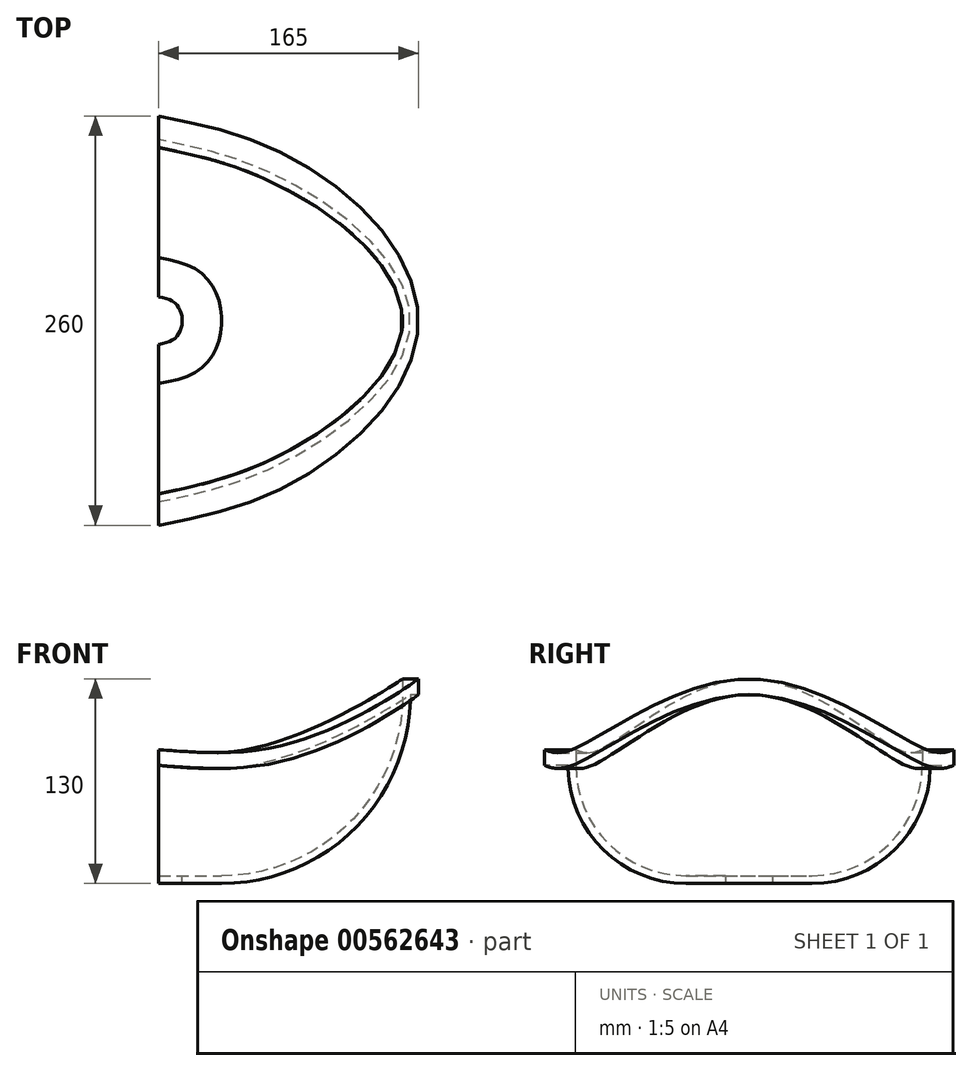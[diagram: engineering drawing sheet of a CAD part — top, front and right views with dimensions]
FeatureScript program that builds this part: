
annotation { "Feature Type Name" : "Feature", "Feature Type Description" : "" }
export const myFeature = defineFeature(function(context is Context, id is Id, definition is map)
    precondition{}
    {
        {
            var Q0;
            Q0=qCreatedBy(makeId("Front.planeOp"),FACE);
            var sketch = newSketch(context, id + "F0", { "sketchPlane" : qUnion([Q0])});
            skLineSegment(sketch, "E0.bottom", {"start": v(15, 5) * mm, "end": v(40, 5) * mm});
            skLineSegment(sketch, "E0.top", {"start": v(15, 0) * mm, "end": v(40, 0) * mm});
            skLineSegment(sketch, "E0.left", {"start": v(15, 5) * mm, "end": v(15, 0) * mm});
            skLineSegment(sketch, "E0.right", {"start": v(40, 5) * mm, "end": v(40, 0) * mm, "construction": true});
            skLineSegment(sketch, "E1.bottom", {"start": v(155, 130) * mm, "end": v(165, 130) * mm});
            skLineSegment(sketch, "E1.top", {"start": v(160, 120) * mm, "end": v(165, 120) * mm});
            skLineSegment(sketch, "E1.left", {"start": v(155, 130) * mm, "end": v(155, 120) * mm});
            skLineSegment(sketch, "E1.right", {"start": v(165, 130) * mm, "end": v(165, 120) * mm});
            skArc(sketch, "E2", {"start": v(40, 0) * mm, "mid": v(124.85, 35.15) * mm, "end": v(160, 120) * mm});
            skArc(sketch, "E3", {"start": v(40, 5) * mm, "mid": v(121.32, 38.68) * mm, "end": v(155, 120) * mm});
            skLineSegment(sketch, "E4", {"start": v(0, 0) * mm, "end": v(0, 50) * mm, "construction": true});
            skSolve(sketch);
        }
        {
            var Q0;
            Q0=sQuery(id+"F0.wireOp",EDGE,"E4");
            cPlane(context, id + "F1", {"entities" : qUnion([Q0]), "cplaneType" : CPlaneType.LINE_ANGLE, "offset" : 25 * mm, "angle" : 30 * degree, "oppositeDirection" : true, "width" : 150 * mm, "height" : 150 * mm});
        }
        {
            var Q0;
            Q0=qCreatedBy(id+"F1.planeOp",FACE);
            var sketch = newSketch(context, id + "F2", { "sketchPlane" : qUnion([Q0])});
            skLineSegment(sketch, "E5.bottom", {"start": v(15, 5) * mm, "end": v(40, 5) * mm});
            skLineSegment(sketch, "E5.top", {"start": v(15, 0) * mm, "end": v(40, 0) * mm});
            skLineSegment(sketch, "E5.left", {"start": v(15, 5) * mm, "end": v(15, 0) * mm});
            skLineSegment(sketch, "E5.right", {"start": v(40, 5) * mm, "end": v(40, 0) * mm, "construction": true});
            skLineSegment(sketch, "E6.bottom", {"start": v(110, 85) * mm, "end": v(130, 85) * mm});
            skLineSegment(sketch, "E6.top", {"start": v(115, 75) * mm, "end": v(130, 75) * mm});
            skLineSegment(sketch, "E6.left", {"start": v(110, 85) * mm, "end": v(110, 75) * mm});
            skLineSegment(sketch, "E6.right", {"start": v(130, 85) * mm, "end": v(130, 75) * mm});
            skArc(sketch, "E7", {"start": v(40, 0) * mm, "mid": v(93.03, 21.97) * mm, "end": v(115, 75) * mm});
            skArc(sketch, "E8", {"start": v(40, 5) * mm, "mid": v(89.5, 25.5) * mm, "end": v(110, 75) * mm});
            skLineSegment(sketch, "E9", {"start": v(0, 0) * mm, "end": v(0, 50) * mm, "construction": true});
            skSolve(sketch);
        }
        {
            var Q0;
            Q0=sQuery(id+"F2.wireOp",EDGE,"E9");
            cPlane(context, id + "F3", {"entities" : qUnion([Q0]), "cplaneType" : CPlaneType.LINE_ANGLE, "offset" : 25 * mm, "angle" : 150 * degree, "oppositeDirection" : true, "width" : 150 * mm, "height" : 150 * mm});
        }
        {
            var Q0;
            Q0=qCreatedBy(id+"F3.planeOp",FACE);
            var sketch = newSketch(context, id + "F4", { "sketchPlane" : qUnion([Q0])});
            skLineSegment(sketch, "E10.bottom", {"start": v(15, 5) * mm, "end": v(40, 5) * mm});
            skLineSegment(sketch, "E10.top", {"start": v(15, 0) * mm, "end": v(40, 0) * mm});
            skLineSegment(sketch, "E10.left", {"start": v(15, 5) * mm, "end": v(15, 0) * mm});
            skLineSegment(sketch, "E10.right", {"start": v(40, 5) * mm, "end": v(40, 0) * mm, "construction": true});
            skLineSegment(sketch, "E11.bottom", {"start": v(110, 85) * mm, "end": v(130, 85) * mm});
            skLineSegment(sketch, "E11.top", {"start": v(115, 75) * mm, "end": v(130, 75) * mm});
            skLineSegment(sketch, "E11.left", {"start": v(110, 85) * mm, "end": v(110, 75) * mm});
            skLineSegment(sketch, "E11.right", {"start": v(130, 85) * mm, "end": v(130, 75) * mm});
            skArc(sketch, "E12", {"start": v(40, 0) * mm, "mid": v(93.03, 21.97) * mm, "end": v(115, 75) * mm});
            skArc(sketch, "E13", {"start": v(40, 5) * mm, "mid": v(89.5, 25.5) * mm, "end": v(110, 75) * mm});
            skLineSegment(sketch, "E14", {"start": v(0, 0) * mm, "end": v(0, 50) * mm, "construction": true});
            skSolve(sketch);
        }
        {
            var Q0;
            Q0=qCreatedBy(makeId("Right.planeOp"),FACE);
            var sketch = newSketch(context, id + "F5", { "sketchPlane" : qUnion([Q0])});
            skLineSegment(sketch, "E15.bottom", {"start": v(15, 5) * mm, "end": v(40, 5) * mm});
            skLineSegment(sketch, "E15.top", {"start": v(15, 0) * mm, "end": v(40, 0) * mm});
            skLineSegment(sketch, "E15.left", {"start": v(15, 5) * mm, "end": v(15, 0) * mm});
            skLineSegment(sketch, "E15.right", {"start": v(40, 5) * mm, "end": v(40, 0) * mm, "construction": true});
            skLineSegment(sketch, "E16.bottom", {"start": v(110, 85) * mm, "end": v(130, 85) * mm});
            skLineSegment(sketch, "E16.top", {"start": v(115, 75) * mm, "end": v(130, 75) * mm});
            skLineSegment(sketch, "E16.left", {"start": v(110, 85) * mm, "end": v(110, 75) * mm});
            skLineSegment(sketch, "E16.right", {"start": v(130, 85) * mm, "end": v(130, 75) * mm});
            skArc(sketch, "E17", {"start": v(40, 0) * mm, "mid": v(93.03, 21.97) * mm, "end": v(115, 75) * mm});
            skArc(sketch, "E18", {"start": v(40, 5) * mm, "mid": v(89.5, 25.5) * mm, "end": v(110, 75) * mm});
            skLineSegment(sketch, "E19", {"start": v(0, 0) * mm, "end": v(0, 50) * mm, "construction": true});
            skSolve(sketch);
        }
        {
            var Q0;
            Q0=sQuery(id+"F5.wireOp",EDGE,"E19");
            cPlane(context, id + "F6", {"entities" : qUnion([Q0]), "cplaneType" : CPlaneType.LINE_ANGLE, "offset" : 25 * mm, "angle" : 180 * degree, "width" : 150 * mm, "height" : 150 * mm});
        }
        {
            var Q0;
            Q0=qCreatedBy(id+"F6.planeOp",FACE);
            var sketch = newSketch(context, id + "F7", { "sketchPlane" : qUnion([Q0])});
            skLineSegment(sketch, "E20.bottom", {"start": v(15, 5) * mm, "end": v(40, 5) * mm});
            skLineSegment(sketch, "E20.top", {"start": v(15, 0) * mm, "end": v(40, 0) * mm});
            skLineSegment(sketch, "E20.left", {"start": v(15, 5) * mm, "end": v(15, 0) * mm});
            skLineSegment(sketch, "E20.right", {"start": v(40, 5) * mm, "end": v(40, 0) * mm, "construction": true});
            skLineSegment(sketch, "E21.bottom", {"start": v(110, 85) * mm, "end": v(130, 85) * mm});
            skLineSegment(sketch, "E21.top", {"start": v(115, 75) * mm, "end": v(130, 75) * mm});
            skLineSegment(sketch, "E21.left", {"start": v(110, 85) * mm, "end": v(110, 75) * mm});
            skLineSegment(sketch, "E21.right", {"start": v(130, 85) * mm, "end": v(130, 75) * mm});
            skArc(sketch, "E22", {"start": v(40, 0) * mm, "mid": v(93.03, 21.97) * mm, "end": v(115, 75) * mm});
            skArc(sketch, "E23", {"start": v(40, 5) * mm, "mid": v(89.5, 25.5) * mm, "end": v(110, 75) * mm});
            skLineSegment(sketch, "E24", {"start": v(0, 0) * mm, "end": v(0, 50) * mm, "construction": true});
            skSolve(sketch);
        }
        {
            var Q0;
            Q0 = qSketchRegion(id + "F7", true);
            var Q1;
            Q1 = qSketchRegion(id + "F4", true);
            var Q2;
            Q2 = qSketchRegion(id + "F0", true);
            var Q3;
            Q3 = qSketchRegion(id + "F2", true);
            var Q4;
            Q4 = qSketchRegion(id + "F5", true);
            loft(context, id + "F8", {"sheetProfilesArray" : [{ "sheetProfileEntities" : qUnion([Q0]) }, { "sheetProfileEntities" : qUnion([Q1]) }, { "sheetProfileEntities" : qUnion([Q2]) }, { "sheetProfileEntities" : qUnion([Q3]) }, { "sheetProfileEntities" : qUnion([Q4]) }]});
        }
    });
